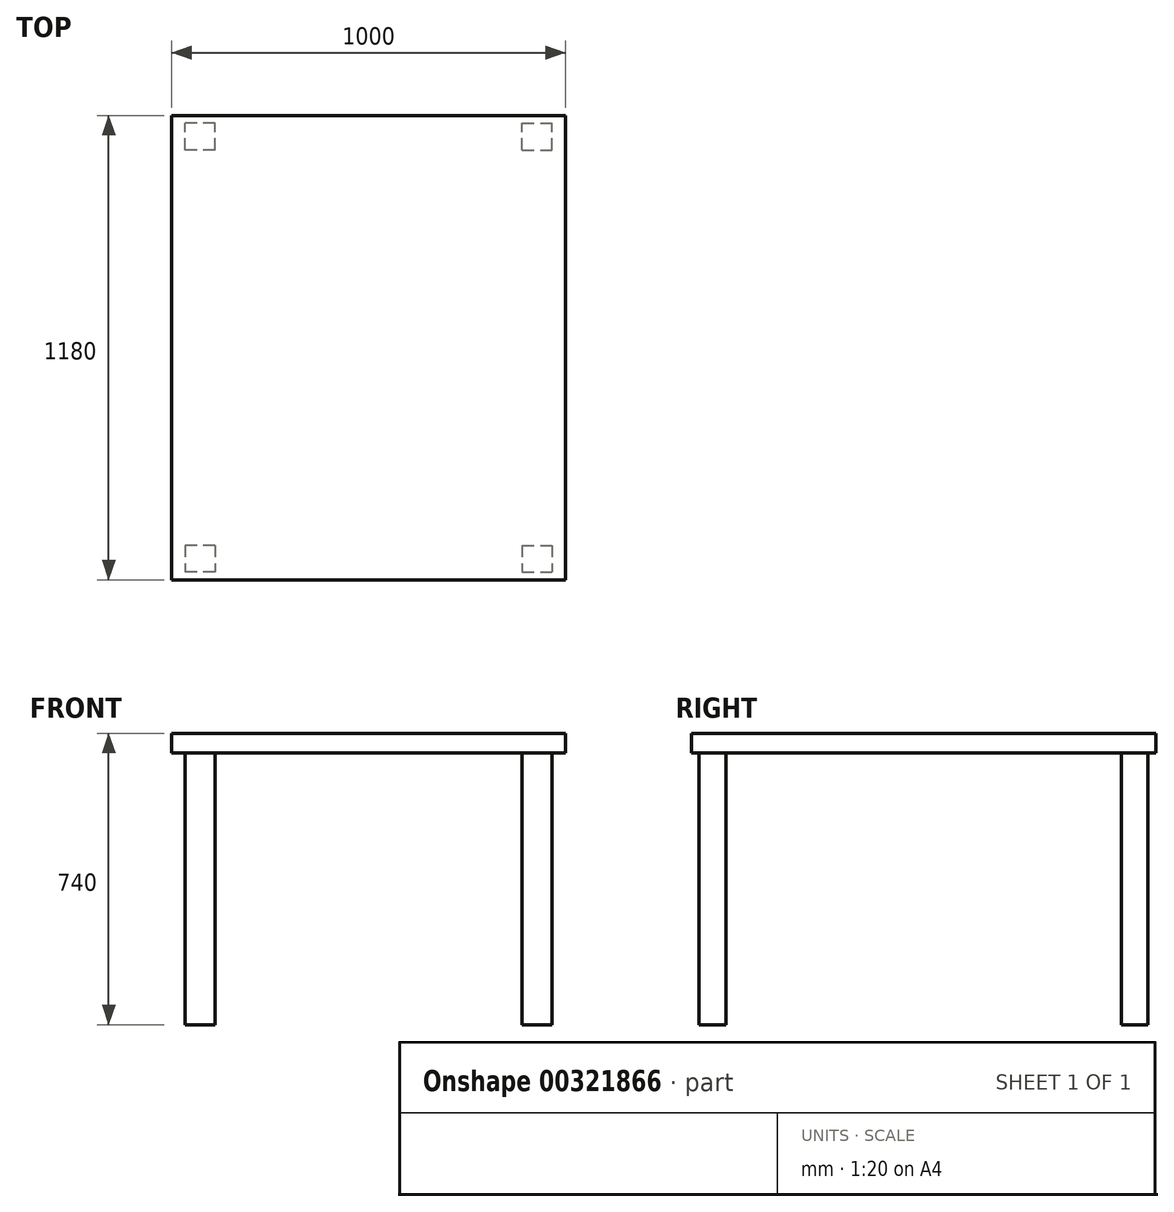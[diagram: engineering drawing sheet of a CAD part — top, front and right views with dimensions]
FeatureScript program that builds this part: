
annotation { "Feature Type Name" : "Feature", "Feature Type Description" : "" }
export const myFeature = defineFeature(function(context is Context, id is Id, definition is map)
    precondition{}
    {
        {
            var Q0;
            Q0=qCreatedBy(makeId("Top.planeOp"),FACE);
            var sketch = newSketch(context, id + "F0", { "sketchPlane" : qUnion([Q0])});
            skLineSegment(sketch, "E0.bottom", {"start": v(500, 590) * mm, "end": v(-500, 590) * mm});
            skLineSegment(sketch, "E0.top", {"start": v(500, -590) * mm, "end": v(-500, -590) * mm});
            skLineSegment(sketch, "E0.left", {"start": v(500, 590) * mm, "end": v(500, -590) * mm});
            skLineSegment(sketch, "E0.right", {"start": v(-500, 590) * mm, "end": v(-500, -590) * mm});
            skPoint(sketch, "E0.middle", {"position": v(0, 0) * mm});
            skSolve(sketch);
        }
        {
            var Q0;
            Q0 = qSketchRegion(id + "F0", true);
            extrude(context, id + "F1", {"entities" : qUnion([Q0]), "oppositeDirection" : true, "depth" : 50 * mm});
        }
        {
            var Q0;
            Q0=makeQuery(id+"F1.opExtrude","CAP_FACE",FACE,{"disambiguationData":[OSD([sQuery(id+"F0.wireOp",EDGE,"E0.bottom"),sQuery(id+"F0.wireOp",EDGE,"E0.top"),sQuery(id+"F0.wireOp",EDGE,"E0.left"),sQuery(id+"F0.wireOp",EDGE,"E0.right")])],"isStart":false});
            var sketch = newSketch(context, id + "F2", { "sketchPlane" : qUnion([Q0])});
            skLineSegment(sketch, "E1", {"start": v(-500, 0) * mm, "end": v(500, 0) * mm, "construction": true});
            skLineSegment(sketch, "E2", {"start": v(0, -590) * mm, "end": v(0, 590) * mm, "construction": true});
            skLineSegment(sketch, "E3.bottom", {"start": v(-390.27, 502.04) * mm, "end": v(-466.05, 502.04) * mm});
            skLineSegment(sketch, "E3.top", {"start": v(-390.27, 570.24) * mm, "end": v(-466.05, 570.24) * mm});
            skLineSegment(sketch, "E3.left", {"start": v(-390.27, 502.04) * mm, "end": v(-390.27, 570.24) * mm});
            skLineSegment(sketch, "E3.right", {"start": v(-466.05, 502.04) * mm, "end": v(-466.05, 570.24) * mm});
            skPoint(sketch, "E3.middle", {"position": v(-428.16, 536.14) * mm});
            skLineSegment(sketch, "E4.MirrorCS", {"start": v(466.05, 502.04) * mm, "end": v(466.05, 570.24) * mm});
            skLineSegment(sketch, "E5.MirrorCS", {"start": v(390.27, 502.04) * mm, "end": v(390.27, 570.24) * mm});
            skLineSegment(sketch, "E6.MirrorCS", {"start": v(390.27, 502.04) * mm, "end": v(466.05, 502.04) * mm});
            skLineSegment(sketch, "E7.MirrorCS", {"start": v(390.27, 570.24) * mm, "end": v(466.05, 570.24) * mm});
            skPoint(sketch, "E8.MirrorP", {"position": v(428.16, 536.14) * mm});
            skLineSegment(sketch, "E9.MirrorCS", {"start": v(466.05, -502.04) * mm, "end": v(466.05, -570.24) * mm});
            skLineSegment(sketch, "E10.MirrorCS", {"start": v(-466.05, -502.04) * mm, "end": v(-466.05, -570.24) * mm});
            skLineSegment(sketch, "E11.MirrorCS", {"start": v(-390.27, -502.04) * mm, "end": v(-390.27, -570.24) * mm});
            skLineSegment(sketch, "E12.MirrorCS", {"start": v(-390.27, -570.24) * mm, "end": v(-466.05, -570.24) * mm});
            skLineSegment(sketch, "E13.MirrorCS", {"start": v(-390.27, -502.04) * mm, "end": v(-466.05, -502.04) * mm});
            skLineSegment(sketch, "E14.MirrorCS", {"start": v(390.27, -502.04) * mm, "end": v(390.27, -570.24) * mm});
            skLineSegment(sketch, "E15.MirrorCS", {"start": v(390.27, -570.24) * mm, "end": v(466.05, -570.24) * mm});
            skLineSegment(sketch, "E16.MirrorCS", {"start": v(390.27, -502.04) * mm, "end": v(466.05, -502.04) * mm});
            skPoint(sketch, "E17.MirrorP", {"position": v(428.16, -536.14) * mm});
            skPoint(sketch, "E18.MirrorP", {"position": v(-428.16, -536.14) * mm});
            skSolve(sketch);
        }
        {
            var Q0;
            Q0 = qSketchRegion(id + "F2", true);
            extrude(context, id + "F3", {"entities" : qUnion([Q0]), "operationType" : NewBodyOperationType.ADD, "depth" : (740 - 50) * mm});
        }
    });
